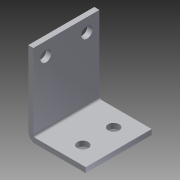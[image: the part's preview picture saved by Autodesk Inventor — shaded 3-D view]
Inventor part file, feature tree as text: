
AUTODESK INVENTOR PART (.ipt)
format: ipt  version: 2013 (Build 170138000, 138)  size: 124,416 bytes
history: native  units: in
note: dims shown in document units (in); Inventor stores cm internally (conversion verified against a paired STEP export)
features: sheet_metal_op x4, sketch x3, other x3
ambient origin geometry x8: Origin, YZ Plane, XZ Plane, XY Plane, X Axis, Y Axis, Z Axis, Center Point
bodies: Solid1 (feature_tree)
feature tree (10):
  sheet_metal_op  "Face1"
  sheet_metal_op  "Flange1"
  sketch  "Sketch1"  dims[d0=1.4in]
  other  "Plate1"
  sketch  "Sketch2"  dims[d2=1.6084in]
  other  "Plate2"
  sheet_metal_op  "Bend1"
  sheet_metal_op  "Corner1"
  sketch  "Sketch3"  dims[d3=0.266in d4=0.75in d5=0.125in d6=0.125in d7=0.0625in d8=0.25in d9=0.125in d10=2.0in d11=90.0deg d12=0.05in d13=0.5in d14=0.125in d15=0.125in d16=0.5in d18=0.266in d19=1.5in d20=1.0in d21=0.125in d22=0.0in]
  other  "Cut1"
